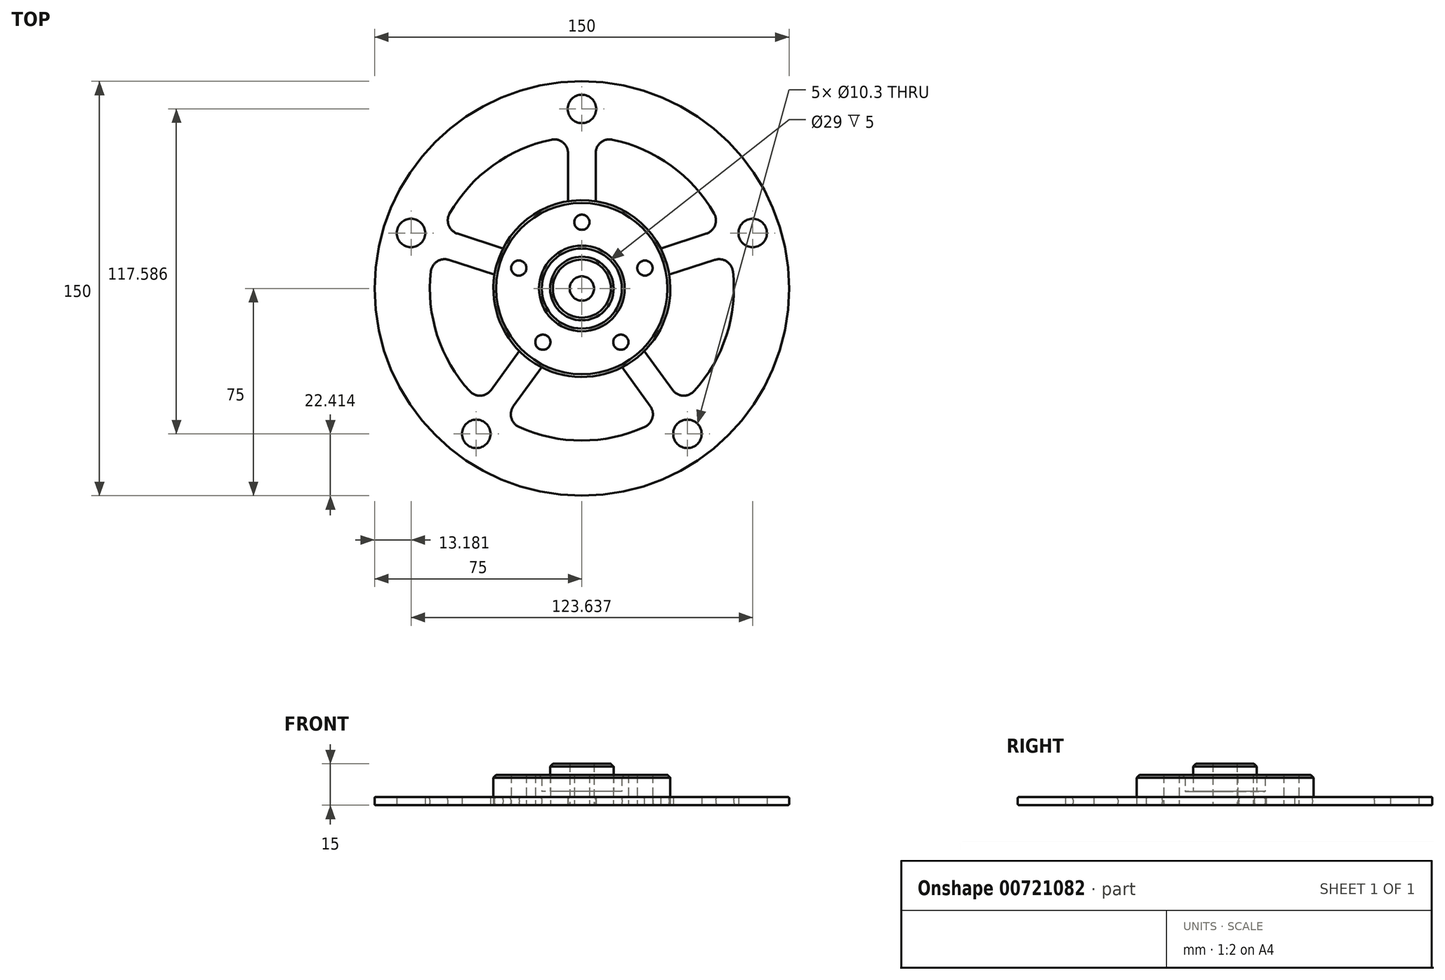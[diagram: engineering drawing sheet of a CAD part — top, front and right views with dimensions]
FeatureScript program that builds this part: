
annotation { "Feature Type Name" : "Feature", "Feature Type Description" : "" }
export const myFeature = defineFeature(function(context is Context, id is Id, definition is map)
    precondition{}
    {
        {
            var Q0;
            Q0=qCreatedBy(makeId("Top.planeOp"),FACE);
            var sketch = newSketch(context, id + "F0", { "sketchPlane" : qUnion([Q0])});
            skCircle(sketch, "E0", {"center": v(0, 0) * mm, "radius": 11.5 * mm});
            skCircle(sketch, "E1", {"center": v(0, 0) * mm, "radius": 14.5 * mm});
            skCircle(sketch, "E2", {"center": v(0, 0) * mm, "radius": 32 * mm});
            skPoint(sketch, "E3", {"position": v(0, 24) * mm});
            skPoint(sketch, "E4.1.0", {"position": v(-22.83, 7.42) * mm});
            skPoint(sketch, "E4.2.0", {"position": v(-14.1, -19.42) * mm});
            skPoint(sketch, "E4.3.0", {"position": v(14.1, -19.42) * mm});
            skPoint(sketch, "E4.4.0", {"position": v(22.83, 7.42) * mm});
            skPoint(sketch, "E5", {"position": v(0, 65) * mm});
            skPoint(sketch, "E6.1.0", {"position": v(-61.82, 20.09) * mm});
            skPoint(sketch, "E6.2.0", {"position": v(-38.2, -52.59) * mm});
            skPoint(sketch, "E6.3.0", {"position": v(38.2, -52.59) * mm});
            skPoint(sketch, "E6.4.0", {"position": v(61.82, 20.09) * mm});
            skCircle(sketch, "E7.0", {"center": v(0, 0) * mm, "radius": 55 * mm});
            skCircle(sketch, "E8.0", {"center": v(0, 0) * mm, "radius": 75 * mm});
            skPoint(sketch, "E9", {"position": v(0, 55) * mm});
            skPoint(sketch, "E10", {"position": v(0, 32) * mm});
            skPoint(sketch, "E11.1.0", {"position": v(-22.63, 22.63) * mm});
            skPoint(sketch, "E11.2.0", {"position": v(-32, 0) * mm});
            skPoint(sketch, "E11.3.0", {"position": v(-22.63, -22.63) * mm});
            skPoint(sketch, "E11.4.0", {"position": v(0, -32) * mm});
            skPoint(sketch, "E11.5.0", {"position": v(22.63, -22.63) * mm});
            skPoint(sketch, "E11.6.0", {"position": v(32, 0) * mm});
            skPoint(sketch, "E11.7.0", {"position": v(22.63, 22.63) * mm});
            skLineSegment(sketch, "E12.0", {"start": v(5, 54.77) * mm, "end": v(5, 31.6) * mm});
            skPoint(sketch, "E13.end.orphan", {"position": v(-5, 24) * mm});
            skPoint(sketch, "E14.end.orphan", {"position": v(5, 24) * mm});
            skLineSegment(sketch, "E15", {"start": v(-5, 54.77) * mm, "end": v(-5, 31.6) * mm});
            skPoint(sketch, "E16.MirrorCS.start.orphan", {"position": v(-5, 55) * mm});
            skPoint(sketch, "E17.orphan", {"position": v(5, 55) * mm});
            skLineSegment(sketch, "E18.1.0", {"start": v(-53.64, 12.17) * mm, "end": v(-31.6, 5.01) * mm});
            skLineSegment(sketch, "E18.1.1", {"start": v(-50.55, 21.68) * mm, "end": v(-28.51, 14.52) * mm});
            skLineSegment(sketch, "E18.2.0", {"start": v(-28.15, -47.25) * mm, "end": v(-14.53, -28.5) * mm});
            skLineSegment(sketch, "E18.2.1", {"start": v(-36.24, -41.37) * mm, "end": v(-22.62, -22.63) * mm});
            skLineSegment(sketch, "E18.3.0", {"start": v(36.24, -41.37) * mm, "end": v(22.62, -22.63) * mm});
            skLineSegment(sketch, "E18.3.1", {"start": v(28.15, -47.25) * mm, "end": v(14.53, -28.5) * mm});
            skLineSegment(sketch, "E18.4.0", {"start": v(50.55, 21.68) * mm, "end": v(28.51, 14.52) * mm});
            skLineSegment(sketch, "E18.4.1", {"start": v(53.64, 12.17) * mm, "end": v(31.6, 5.01) * mm});
            skSolve(sketch);
        }
        {
            var Q0;
            Q0=makeQuery(id+"F0.imprint","IMPRINT",FACE,{"disambiguationData":[TD([[makeQuery(id+"F0.imprint","IMPRINT",EDGE,{"derivedFrom":sQuery(id+"F0.wireOp",EDGE,"E0")}),1.0]])]});
            extrude(context, id + "F1", {"entities" : qUnion([Q0]), "depth" : 15 * mm, "offsetDistance" : 25 * mm});
        }
        {
            var Q0;
            Q0=makeQuery(id+"F0.imprint","IMPRINT",FACE,{"disambiguationData":[TD([[makeQuery(id+"F0.imprint","IMPRINT",EDGE,{"derivedFrom":sQuery(id+"F0.wireOp",EDGE,"E0")}),-1.0]])]});
            extrude(context, id + "F2", {"entities" : qUnion([Q0]), "operationType" : NewBodyOperationType.ADD, "depth" : 5 * mm, "offsetDistance" : 25 * mm});
        }
        {
            var Q0;
            Q0=makeQuery(id+"F0.imprint","IMPRINT",FACE,{"disambiguationData":[TD([[makeQuery(id+"F0.imprint","IMPRINT",EDGE,{"derivedFrom":sQuery(id+"F0.wireOp",EDGE,"E1")}),-1.0]])]});
            extrude(context, id + "F3", {"entities" : qUnion([Q0]), "operationType" : NewBodyOperationType.ADD, "depth" : 11 * mm, "offsetDistance" : 25 * mm});
        }
        {
            var Q0;
            Q0=sQuery(id+"F0.wireOp",VERTEX,"E4.1.0");
            var Q1;
            Q1=sQuery(id+"F0.wireOp",VERTEX,"E3");
            var Q2;
            Q2=sQuery(id+"F0.wireOp",VERTEX,"E4.4.0");
            var Q3;
            Q3=sQuery(id+"F0.wireOp",VERTEX,"E4.3.0");
            var Q4;
            Q4=sQuery(id+"F0.wireOp",VERTEX,"E4.2.0");
            var Q5;
            Q5=makeQuery(id+"F1.opExtrude","SWEPT_BODY",BODY,{"disambiguationData":[OSD([sQuery(id+"F0.wireOp",EDGE,"E0")])]});
            hole(context, id + "F4", {"style" : HoleStyle.SIMPLE, "endStyle" : HoleEndStyle.THROUGH, "oppositeDirection" : true, "standardTappedOrClearance" : lookupTablePath({ "standard" : "ISO", "fit" : "Normal", "size" : "M5", "type" : "Clearance" }), "standardBlindInLast" : lookupTablePath({ "fit" : "Standard", "standard" : "ISO", "size" : "M5", "type" : "Clearance" }), "holeDiameter" : 5.5 * mm, "majorDiameter" : 5 * mm, "isTappedThrough" : true, "tappedDepth" : 12 * mm, "tapClearance" : 3, "locations" : qUnion([Q0, Q1, Q2, Q3, Q4]), "scope" : qUnion([Q5])});
        }
        {
            var Q0;
            Q0=sQuery(id+"F0.wireOp",VERTEX,"E0.center");
            var Q1;
            Q1=makeQuery(id+"F1.opExtrude","SWEPT_BODY",BODY,{"disambiguationData":[OSD([sQuery(id+"F0.wireOp",EDGE,"E0")])]});
            hole(context, id + "F5", {"style" : HoleStyle.SIMPLE, "endStyle" : HoleEndStyle.THROUGH, "oppositeDirection" : true, "standardTappedOrClearance" : lookupTablePath({ "standard" : "ISO", "fit" : "Normal", "size" : "M8", "type" : "Clearance" }), "standardBlindInLast" : lookupTablePath({ "fit" : "Standard", "standard" : "ISO", "size" : "M8", "type" : "Clearance" }), "holeDiameter" : 8.8 * mm, "majorDiameter" : 5 * mm, "isTappedThrough" : true, "tappedDepth" : 12 * mm, "tapClearance" : 3, "locations" : qUnion([Q0]), "scope" : qUnion([Q1])});
        }
        {
            var Q0;
            Q0=makeQuery(id+"F1.opExtrude","CAP_EDGE",EDGE,{"disambiguationData":[OSD([sQuery(id+"F0.wireOp",EDGE,"E0")])],"isStart":false});
            chamfer(context, id + "F6", {"entities" : qUnion([Q0]), "width" : 1 * mm, "tangentPropagation" : true});
        }
        {
            var Q0;
            Q0=makeQuery(id+"F3.opExtrude","CAP_EDGE",EDGE,{"disambiguationData":[OSD([sQuery(id+"F0.wireOp",EDGE,"E1")])],"isStart":false});
            chamfer(context, id + "F7", {"entities" : qUnion([Q0]), "width" : 1 * mm, "tangentPropagation" : true});
        }
        {
            var Q0;
            Q0=makeQuery(id+"F3.opExtrude","CAP_EDGE",EDGE,{"disambiguationData":[OSD([sQuery(id+"F0.wireOp",EDGE,"E2")])],"isStart":false});
            chamfer(context, id + "F8", {"entities" : qUnion([Q0]), "width" : 1 * mm, "tangentPropagation" : true});
        }
        {
            var Q0;
            Q0=makeQuery(id+"F0.imprint","IMPRINT",FACE,{"disambiguationData":[TD([[makeQuery(id+"F0.imprint","IMPRINT",EDGE,{"derivedFrom":sQuery(id+"F0.wireOp",EDGE,"E8.0")}),1.0]])]});
            var Q1;
            {var subQ0=sQuery(id+"F0.wireOp",EDGE,"E12.0");Q1=makeQuery(id+"F0.imprint","IMPRINT",FACE,{"disambiguationData":[TD([[makeQuery(id+"F0.imprint","IMPRINT",EDGE,{"derivedFrom":subQ0}),-1.0]])]});}
            var Q2;
            {var subQ0=sQuery(id+"F0.wireOp",EDGE,"E18.1.0");Q2=makeQuery(id+"F0.imprint","IMPRINT",FACE,{"disambiguationData":[TD([[makeQuery(id+"F0.imprint","IMPRINT",EDGE,{"derivedFrom":subQ0}),1.0]])]});}
            var Q3;
            {var subQ0=sQuery(id+"F0.wireOp",EDGE,"E18.2.0");Q3=makeQuery(id+"F0.imprint","IMPRINT",FACE,{"disambiguationData":[TD([[makeQuery(id+"F0.imprint","IMPRINT",EDGE,{"derivedFrom":subQ0}),1.0]])]});}
            var Q4;
            {var subQ0=sQuery(id+"F0.wireOp",EDGE,"E18.3.0");Q4=makeQuery(id+"F0.imprint","IMPRINT",FACE,{"disambiguationData":[TD([[makeQuery(id+"F0.imprint","IMPRINT",EDGE,{"derivedFrom":subQ0}),1.0]])]});}
            var Q5;
            {var subQ0=sQuery(id+"F0.wireOp",EDGE,"E18.4.0");Q5=makeQuery(id+"F0.imprint","IMPRINT",FACE,{"disambiguationData":[TD([[makeQuery(id+"F0.imprint","IMPRINT",EDGE,{"derivedFrom":subQ0}),1.0]])]});}
            extrude(context, id + "F9", {"entities" : qUnion([Q0, Q1, Q2, Q3, Q4, Q5]), "operationType" : NewBodyOperationType.ADD, "depth" : 3 * mm, "offsetDistance" : 25 * mm});
        }
        {
            var Q0;
            Q0=makeQuery(id+"F9.opExtrude","SWEPT_EDGE",EDGE,{"disambiguationData":[OSD([sQuery(id+"F0.wireOp",EDGE,"E7.0"),sQuery(id+"F0.wireOp",EDGE,"E15")])]});
            var Q1;
            Q1=makeQuery(id+"F9.opExtrude","SWEPT_EDGE",EDGE,{"disambiguationData":[OSD([sQuery(id+"F0.wireOp",EDGE,"E2"),sQuery(id+"F0.wireOp",EDGE,"E18.1.0")])]});
            var Q2;
            Q2=makeQuery(id+"F9.opExtrude","SWEPT_EDGE",EDGE,{"disambiguationData":[OSD([sQuery(id+"F0.wireOp",EDGE,"E7.0"),sQuery(id+"F0.wireOp",EDGE,"E18.1.1")])]});
            var Q3;
            Q3=makeQuery(id+"F9.opExtrude","SWEPT_EDGE",EDGE,{"disambiguationData":[OSD([sQuery(id+"F0.wireOp",EDGE,"E2"),sQuery(id+"F0.wireOp",EDGE,"E18.1.1")])]});
            var Q4;
            Q4=makeQuery(id+"F9.opExtrude","SWEPT_EDGE",EDGE,{"disambiguationData":[OSD([sQuery(id+"F0.wireOp",EDGE,"E2"),sQuery(id+"F0.wireOp",EDGE,"E12.0")])]});
            var Q5;
            Q5=makeQuery(id+"F9.opExtrude","SWEPT_EDGE",EDGE,{"disambiguationData":[OSD([sQuery(id+"F0.wireOp",EDGE,"E7.0"),sQuery(id+"F0.wireOp",EDGE,"E12.0")])]});
            var Q6;
            Q6=makeQuery(id+"F9.opExtrude","SWEPT_EDGE",EDGE,{"disambiguationData":[OSD([sQuery(id+"F0.wireOp",EDGE,"E2"),sQuery(id+"F0.wireOp",EDGE,"E18.4.0")])]});
            var Q7;
            Q7=makeQuery(id+"F9.opExtrude","SWEPT_EDGE",EDGE,{"disambiguationData":[OSD([sQuery(id+"F0.wireOp",EDGE,"E7.0"),sQuery(id+"F0.wireOp",EDGE,"E18.4.0")])]});
            var Q8;
            Q8=makeQuery(id+"F9.opExtrude","SWEPT_EDGE",EDGE,{"disambiguationData":[OSD([sQuery(id+"F0.wireOp",EDGE,"E7.0"),sQuery(id+"F0.wireOp",EDGE,"E18.4.1")])]});
            var Q9;
            Q9=makeQuery(id+"F9.opExtrude","SWEPT_EDGE",EDGE,{"disambiguationData":[OSD([sQuery(id+"F0.wireOp",EDGE,"E2"),sQuery(id+"F0.wireOp",EDGE,"E18.4.1")])]});
            var Q10;
            Q10=makeQuery(id+"F9.opExtrude","SWEPT_EDGE",EDGE,{"disambiguationData":[OSD([sQuery(id+"F0.wireOp",EDGE,"E2"),sQuery(id+"F0.wireOp",EDGE,"E18.3.0")])]});
            var Q11;
            Q11=makeQuery(id+"F9.opExtrude","SWEPT_EDGE",EDGE,{"disambiguationData":[OSD([sQuery(id+"F0.wireOp",EDGE,"E2"),sQuery(id+"F0.wireOp",EDGE,"E18.2.0")])]});
            var Q12;
            Q12=makeQuery(id+"F9.opExtrude","SWEPT_EDGE",EDGE,{"disambiguationData":[OSD([sQuery(id+"F0.wireOp",EDGE,"E7.0"),sQuery(id+"F0.wireOp",EDGE,"E18.3.0")])]});
            var Q13;
            Q13=makeQuery(id+"F9.opExtrude","SWEPT_EDGE",EDGE,{"disambiguationData":[OSD([sQuery(id+"F0.wireOp",EDGE,"E7.0"),sQuery(id+"F0.wireOp",EDGE,"E18.3.1")])]});
            var Q14;
            Q14=makeQuery(id+"F9.opExtrude","SWEPT_EDGE",EDGE,{"disambiguationData":[OSD([sQuery(id+"F0.wireOp",EDGE,"E7.0"),sQuery(id+"F0.wireOp",EDGE,"E18.2.0")])]});
            var Q15;
            Q15=makeQuery(id+"F9.opExtrude","SWEPT_EDGE",EDGE,{"disambiguationData":[OSD([sQuery(id+"F0.wireOp",EDGE,"E7.0"),sQuery(id+"F0.wireOp",EDGE,"E18.2.1")])]});
            var Q16;
            Q16=makeQuery(id+"F9.opExtrude","SWEPT_EDGE",EDGE,{"disambiguationData":[OSD([sQuery(id+"F0.wireOp",EDGE,"E2"),sQuery(id+"F0.wireOp",EDGE,"E18.2.1")])]});
            var Q17;
            Q17=makeQuery(id+"F9.opExtrude","SWEPT_EDGE",EDGE,{"disambiguationData":[OSD([sQuery(id+"F0.wireOp",EDGE,"E7.0"),sQuery(id+"F0.wireOp",EDGE,"E18.1.0")])]});
            var Q18;
            {var subQ0=sQuery(id+"F0.wireOp",EDGE,"E2");Q18=makeQuery(id+"F9.opExtrude","CAP_EDGE",EDGE,{"disambiguationData":[OSD([subQ0]),TDD([makeQuery(id+"F0.imprint","IMPRINT",EDGE,{"disambiguationData":[TD([[makeQuery(id+"F0.imprint","INTERSECT",VERTEX,{"derivedFrom":[subQ0,sQuery(id+"F0.wireOp",EDGE,"E18.1.0")]}),1.0]])],"derivedFrom":subQ0})])],"isStart":false});}
            var Q19;
            Q19=makeQuery(id+"F9.opExtrude","SWEPT_EDGE",EDGE,{"disambiguationData":[OSD([sQuery(id+"F0.wireOp",EDGE,"E2"),sQuery(id+"F0.wireOp",EDGE,"E15")])]});
            var Q20;
            {var subQ0=sQuery(id+"F0.wireOp",EDGE,"E2");Q20=makeQuery(id+"F9.opExtrude","CAP_EDGE",EDGE,{"disambiguationData":[OSD([subQ0]),TDD([makeQuery(id+"F0.imprint","IMPRINT",EDGE,{"disambiguationData":[TD([[makeQuery(id+"F0.imprint","INTERSECT",VERTEX,{"derivedFrom":[subQ0,sQuery(id+"F0.wireOp",EDGE,"E12.0")]}),-1.0]])],"derivedFrom":subQ0})])],"isStart":false});}
            var Q21;
            {var subQ0=sQuery(id+"F0.wireOp",EDGE,"E2");Q21=makeQuery(id+"F9.opExtrude","CAP_EDGE",EDGE,{"disambiguationData":[OSD([subQ0]),TDD([makeQuery(id+"F0.imprint","IMPRINT",EDGE,{"disambiguationData":[TD([[makeQuery(id+"F0.imprint","INTERSECT",VERTEX,{"derivedFrom":[subQ0,sQuery(id+"F0.wireOp",EDGE,"E18.4.0")]}),1.0]])],"derivedFrom":subQ0})])],"isStart":false});}
            var Q22;
            {var subQ0=sQuery(id+"F0.wireOp",EDGE,"E2");Q22=makeQuery(id+"F9.opExtrude","CAP_EDGE",EDGE,{"disambiguationData":[OSD([subQ0]),TDD([makeQuery(id+"F0.imprint","IMPRINT",EDGE,{"disambiguationData":[TD([[makeQuery(id+"F0.imprint","INTERSECT",VERTEX,{"derivedFrom":[subQ0,sQuery(id+"F0.wireOp",EDGE,"E18.3.0")]}),1.0]])],"derivedFrom":subQ0})])],"isStart":false});}
            var Q23;
            {var subQ0=sQuery(id+"F0.wireOp",EDGE,"E2");Q23=makeQuery(id+"F9.opExtrude","CAP_EDGE",EDGE,{"disambiguationData":[OSD([subQ0]),TDD([makeQuery(id+"F0.imprint","IMPRINT",EDGE,{"disambiguationData":[TD([[makeQuery(id+"F0.imprint","INTERSECT",VERTEX,{"derivedFrom":[subQ0,sQuery(id+"F0.wireOp",EDGE,"E18.2.0")]}),1.0]])],"derivedFrom":subQ0})])],"isStart":false});}
            var Q24;
            Q24=makeQuery(id+"F9.opExtrude","SWEPT_EDGE",EDGE,{"disambiguationData":[OSD([sQuery(id+"F0.wireOp",EDGE,"E2"),sQuery(id+"F0.wireOp",EDGE,"E18.3.1")])]});
            fillet(context, id + "F10", {"entities" : qUnion([Q0, Q1, Q2, Q3, Q4, Q5, Q6, Q7, Q8, Q9, Q10, Q11, Q12, Q13, Q14, Q15, Q16, Q17, Q18, Q19, Q20, Q21, Q22, Q23, Q24]), "radius" : 5 * mm, "tangentPropagation" : true, "allowEdgeOverflow" : false});
        }
        {
            var Q0;
            {var subQ0=sQuery(id+"F0.wireOp",EDGE,"E7.0");Q0=makeQuery(id+"F9.opExtrude","CAP_EDGE",EDGE,{"disambiguationData":[OSD([subQ0]),TDD([makeQuery(id+"F0.imprint","IMPRINT",EDGE,{"disambiguationData":[TD([[makeQuery(id+"F0.imprint","INTERSECT",VERTEX,{"derivedFrom":[subQ0,sQuery(id+"F0.wireOp",EDGE,"E15")]}),-1.0]])],"derivedFrom":subQ0})])],"isStart":false});}
            var Q1;
            {var subQ0=sQuery(id+"F0.wireOp",EDGE,"E7.0");Q1=makeQuery(id+"F9.opExtrude","CAP_EDGE",EDGE,{"disambiguationData":[OSD([subQ0]),TDD([makeQuery(id+"F0.imprint","IMPRINT",EDGE,{"disambiguationData":[TD([[makeQuery(id+"F0.imprint","INTERSECT",VERTEX,{"derivedFrom":[subQ0,sQuery(id+"F0.wireOp",EDGE,"E12.0")]}),1.0]])],"derivedFrom":subQ0})])],"isStart":false});}
            var Q2;
            {var subQ0=sQuery(id+"F0.wireOp",EDGE,"E7.0");Q2=makeQuery(id+"F9.opExtrude","CAP_EDGE",EDGE,{"disambiguationData":[OSD([subQ0]),TDD([makeQuery(id+"F0.imprint","IMPRINT",EDGE,{"disambiguationData":[TD([[makeQuery(id+"F0.imprint","INTERSECT",VERTEX,{"derivedFrom":[subQ0,sQuery(id+"F0.wireOp",EDGE,"E18.3.0")]}),-1.0]])],"derivedFrom":subQ0})])],"isStart":false});}
            var Q3;
            {var subQ0=sQuery(id+"F0.wireOp",EDGE,"E7.0");Q3=makeQuery(id+"F9.opExtrude","CAP_EDGE",EDGE,{"disambiguationData":[OSD([subQ0]),TDD([makeQuery(id+"F0.imprint","IMPRINT",EDGE,{"disambiguationData":[TD([[makeQuery(id+"F0.imprint","INTERSECT",VERTEX,{"derivedFrom":[subQ0,sQuery(id+"F0.wireOp",EDGE,"E18.2.0")]}),-1.0]])],"derivedFrom":subQ0})])],"isStart":false});}
            var Q4;
            {var subQ0=sQuery(id+"F0.wireOp",EDGE,"E7.0");Q4=makeQuery(id+"F9.opExtrude","CAP_EDGE",EDGE,{"disambiguationData":[OSD([subQ0]),TDD([makeQuery(id+"F0.imprint","IMPRINT",EDGE,{"disambiguationData":[TD([[makeQuery(id+"F0.imprint","INTERSECT",VERTEX,{"derivedFrom":[subQ0,sQuery(id+"F0.wireOp",EDGE,"E18.1.0")]}),-1.0]])],"derivedFrom":subQ0})])],"isStart":false});}
            var Q5;
            {var subQ0=sQuery(id+"F0.wireOp",EDGE,"E7.0");Q5=makeQuery(id+"F9.opExtrude","CAP_EDGE",EDGE,{"disambiguationData":[OSD([subQ0]),TDD([makeQuery(id+"F0.imprint","IMPRINT",EDGE,{"disambiguationData":[TD([[makeQuery(id+"F0.imprint","INTERSECT",VERTEX,{"derivedFrom":[subQ0,sQuery(id+"F0.wireOp",EDGE,"E12.0")]}),1.0]])],"derivedFrom":subQ0})])],"isStart":true});}
            var Q6;
            {var subQ0=sQuery(id+"F0.wireOp",EDGE,"E7.0");Q6=makeQuery(id+"F9.opExtrude","CAP_EDGE",EDGE,{"disambiguationData":[OSD([subQ0]),TDD([makeQuery(id+"F0.imprint","IMPRINT",EDGE,{"disambiguationData":[TD([[makeQuery(id+"F0.imprint","INTERSECT",VERTEX,{"derivedFrom":[subQ0,sQuery(id+"F0.wireOp",EDGE,"E18.3.0")]}),-1.0]])],"derivedFrom":subQ0})])],"isStart":true});}
            var Q7;
            {var subQ0=sQuery(id+"F0.wireOp",EDGE,"E7.0");Q7=makeQuery(id+"F9.opExtrude","CAP_EDGE",EDGE,{"disambiguationData":[OSD([subQ0]),TDD([makeQuery(id+"F0.imprint","IMPRINT",EDGE,{"disambiguationData":[TD([[makeQuery(id+"F0.imprint","INTERSECT",VERTEX,{"derivedFrom":[subQ0,sQuery(id+"F0.wireOp",EDGE,"E18.2.0")]}),-1.0]])],"derivedFrom":subQ0})])],"isStart":true});}
            var Q8;
            {var subQ0=sQuery(id+"F0.wireOp",EDGE,"E7.0");Q8=makeQuery(id+"F9.opExtrude","CAP_EDGE",EDGE,{"disambiguationData":[OSD([subQ0]),TDD([makeQuery(id+"F0.imprint","IMPRINT",EDGE,{"disambiguationData":[TD([[makeQuery(id+"F0.imprint","INTERSECT",VERTEX,{"derivedFrom":[subQ0,sQuery(id+"F0.wireOp",EDGE,"E18.1.0")]}),-1.0]])],"derivedFrom":subQ0})])],"isStart":true});}
            var Q9;
            {var subQ0=sQuery(id+"F0.wireOp",EDGE,"E7.0");Q9=makeQuery(id+"F9.opExtrude","CAP_EDGE",EDGE,{"disambiguationData":[OSD([subQ0]),TDD([makeQuery(id+"F0.imprint","IMPRINT",EDGE,{"disambiguationData":[TD([[makeQuery(id+"F0.imprint","INTERSECT",VERTEX,{"derivedFrom":[subQ0,sQuery(id+"F0.wireOp",EDGE,"E15")]}),-1.0]])],"derivedFrom":subQ0})])],"isStart":true});}
            fillet(context, id + "F11", {"entities" : qUnion([Q0, Q1, Q2, Q3, Q4, Q5, Q6, Q7, Q8, Q9]), "radius" : 1 * mm, "tangentPropagation" : true, "allowEdgeOverflow" : false});
        }
        {
            var Q0;
            Q0=makeQuery(id+"F9.opExtrude","CAP_EDGE",EDGE,{"disambiguationData":[OSD([sQuery(id+"F0.wireOp",EDGE,"E8.0")])],"isStart":false});
            fillet(context, id + "F12", {"entities" : qUnion([Q0]), "radius" : 0.5 * mm, "tangentPropagation" : true, "allowEdgeOverflow" : false});
        }
        {
            var Q0;
            Q0=makeQuery(id+"F9.opExtrude","CAP_EDGE",EDGE,{"disambiguationData":[OSD([sQuery(id+"F0.wireOp",EDGE,"E8.0")])],"isStart":true});
            fillet(context, id + "F13", {"entities" : qUnion([Q0]), "radius" : 0.5 * mm, "tangentPropagation" : true, "allowEdgeOverflow" : false});
        }
        {
            var Q0;
            Q0=sQuery(id+"F0.wireOp",VERTEX,"E6.1.0");
            var Q1;
            Q1=sQuery(id+"F0.wireOp",VERTEX,"E5");
            var Q2;
            Q2=sQuery(id+"F0.wireOp",VERTEX,"E6.4.0");
            var Q3;
            Q3=sQuery(id+"F0.wireOp",VERTEX,"E6.3.0");
            var Q4;
            Q4=sQuery(id+"F0.wireOp",VERTEX,"E6.2.0");
            var Q5;
            Q5=makeQuery(id+"F1.opExtrude","SWEPT_BODY",BODY,{"disambiguationData":[OSD([sQuery(id+"F0.wireOp",EDGE,"E0")])]});
            hole(context, id + "F14", {"style" : HoleStyle.SIMPLE, "endStyle" : HoleEndStyle.THROUGH, "oppositeDirection" : true, "holeDiameter" : 10.3 * mm, "majorDiameter" : 5 * mm, "isTappedThrough" : true, "tappedDepth" : 48.5 * mm, "tapClearance" : 3, "locations" : qUnion([Q0, Q1, Q2, Q3, Q4]), "scope" : qUnion([Q5])});
        }
    });
